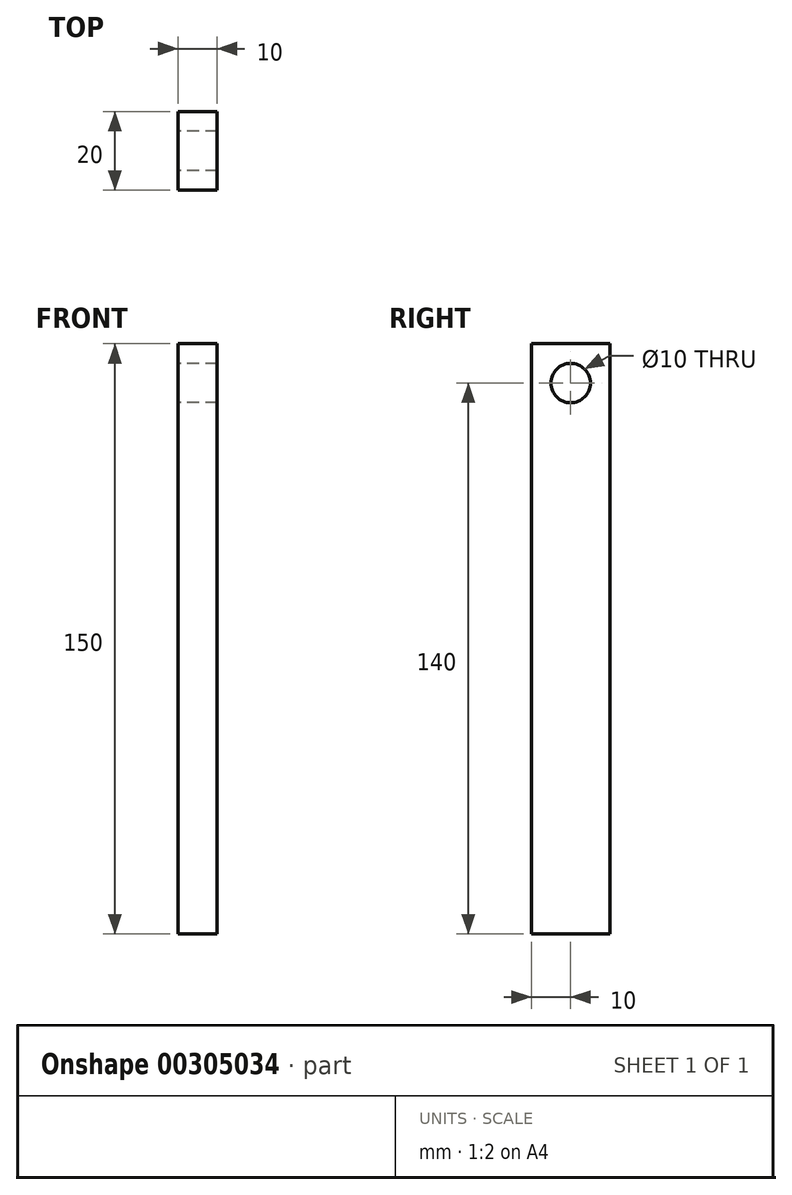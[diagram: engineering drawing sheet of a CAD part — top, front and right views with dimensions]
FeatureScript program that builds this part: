
annotation { "Feature Type Name" : "Feature", "Feature Type Description" : "" }
export const myFeature = defineFeature(function(context is Context, id is Id, definition is map)
    precondition{}
    {
        {
            var Q0;
            Q0=qCreatedBy(makeId("Right.planeOp"),FACE);
            var sketch = newSketch(context, id + "F0", { "sketchPlane" : qUnion([Q0])});
            skLineSegment(sketch, "E0.bottom", {"start": v(0, 0) * mm, "end": v(20, 0) * mm});
            skLineSegment(sketch, "E0.top", {"start": v(0, 150) * mm, "end": v(20, 150) * mm});
            skLineSegment(sketch, "E0.left", {"start": v(0, 0) * mm, "end": v(0, 150) * mm});
            skLineSegment(sketch, "E0.right", {"start": v(20, 0) * mm, "end": v(20, 150) * mm});
            skCircle(sketch, "E1", {"center": v(10, 140) * mm, "radius": 5 * mm});
            skSolve(sketch);
        }
        {
            var Q0;
            Q0=makeQuery(id+"F0.imprint","IMPRINT",FACE,{"disambiguationData":[TD([[makeQuery(id+"F0.imprint","IMPRINT",EDGE,{"derivedFrom":sQuery(id+"F0.wireOp",EDGE,"E0.bottom")}),1.0]])]});
            extrude(context, id + "F1", {"entities" : qUnion([Q0]), "depth" : 10 * mm});
        }
    });
